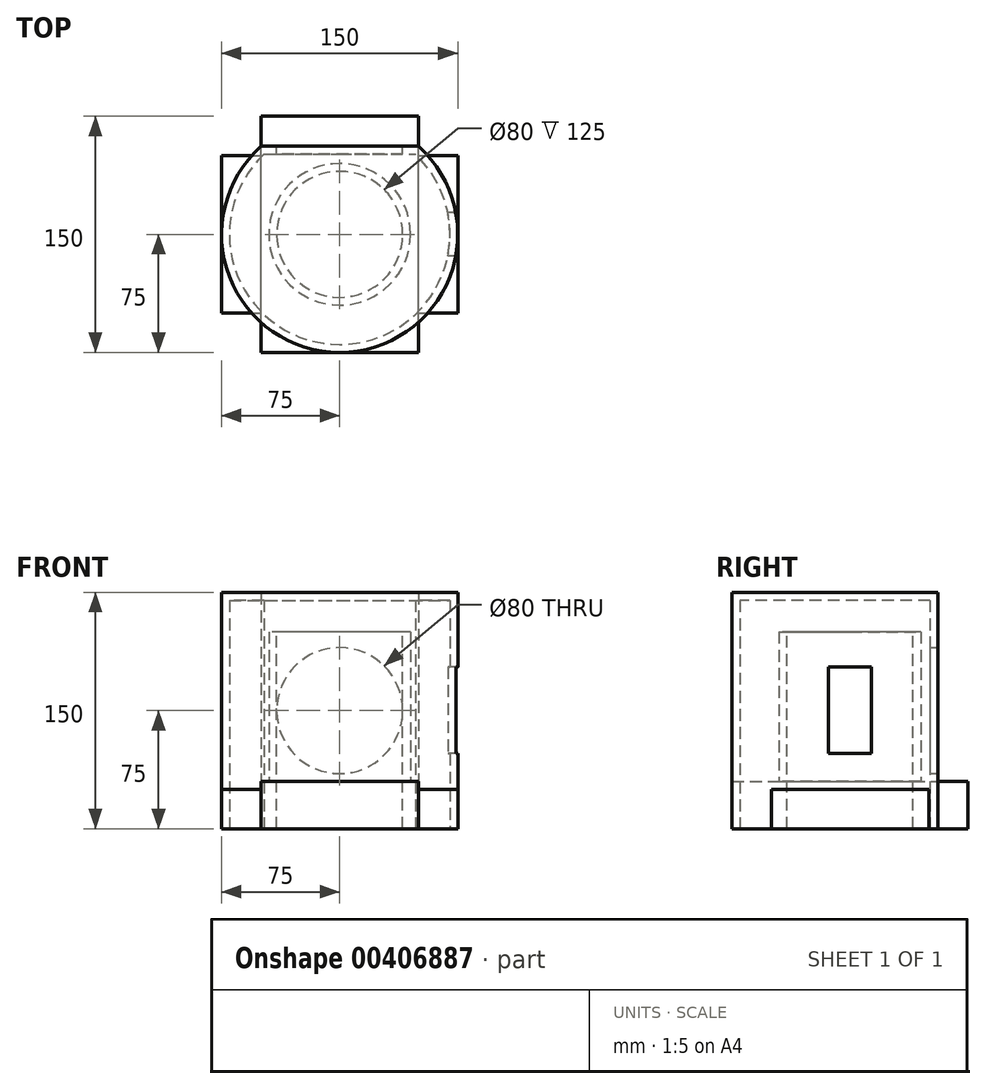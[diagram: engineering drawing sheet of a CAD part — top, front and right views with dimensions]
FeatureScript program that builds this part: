
annotation { "Feature Type Name" : "Feature", "Feature Type Description" : "" }
export const myFeature = defineFeature(function(context is Context, id is Id, definition is map)
    precondition{}
    {
        {
            var Q0;
            Q0=qCreatedBy(makeId("Top.planeOp"),FACE);
            var sketch = newSketch(context, id + "F0", { "sketchPlane" : qUnion([Q0])});
            skArc(sketch, "E0", {"start": v(-50, 55.9) * mm, "mid": v(0, -75) * mm, "end": v(50, 55.9) * mm});
            skLineSegment(sketch, "E1", {"start": v(-50, 55.9) * mm, "end": v(50, 55.9) * mm});
            skSolve(sketch);
        }
        {
            var Q0;
            Q0=qSketchRegion(id+"F0",true);
            extrude(context, id + "F1", {"entities" : qUnion([Q0]), "depth" : 150 * mm});
        }
        {
            var Q0;
            Q0=makeQuery(id+"F1.opExtrude","CAP_FACE",FACE,{"disambiguationData":[OSD([sQuery(id+"F0.wireOp",EDGE,"E0")])],"isStart":true});
            shell(context, id + "F2", {"entities" : qUnion([Q0]), "thickness" : 5 * mm});
        }
        {
            var Q0;
            Q0=makeQuery(id+"F1.opExtrude","SWEPT_FACE",FACE,{"disambiguationData":[OSD([sQuery(id+"F0.wireOp",EDGE,"E1")])]});
            var sketch = newSketch(context, id + "F3", { "sketchPlane" : qUnion([Q0])});
            skPoint(sketch, "E2.endSnap0", {"position": v(0, 0) * mm});
            skCircle(sketch, "E3", {"center": v(0, 75) * mm, "radius": 40 * mm});
            skLineSegment(sketch, "E4", {"start": v(0, 115) * mm, "end": v(0, 150) * mm});
            skSolve(sketch);
        }
        {
            var Q0;
            Q0=qSketchRegion(id+"F3",true);
            extrude(context, id + "F4", {"entities" : qUnion([Q0]), "operationType" : NewBodyOperationType.REMOVE, "oppositeDirection" : true, "depth" : 25 * mm});
        }
        {
            var Q0;
            Q0=qCreatedBy(makeId("Top.planeOp"),FACE);
            var sketch = newSketch(context, id + "F5", { "sketchPlane" : qUnion([Q0])});
            skLineSegment(sketch, "E5.bottom", {"start": v(-50, -75) * mm, "end": v(50, -75) * mm});
            skLineSegment(sketch, "E5.top", {"start": v(-50, 75) * mm, "end": v(50, 75) * mm});
            skLineSegment(sketch, "E5.left", {"start": v(-50, -75) * mm, "end": v(-50, 75) * mm});
            skLineSegment(sketch, "E5.right", {"start": v(50, -75) * mm, "end": v(50, 75) * mm});
            skPoint(sketch, "E5.middle", {"position": v(0, 0) * mm});
            skSolve(sketch);
        }
        {
            var Q0;
            Q0=qSketchRegion(id+"F5",true);
            extrude(context, id + "F6", {"entities" : qUnion([Q0]), "depth" : 30 * mm});
        }
        {
            var Q0;
            Q0=makeQuery(id+"F6.opExtrude","CAP_FACE",FACE,{"disambiguationData":[OSD([sQuery(id+"F5.wireOp",EDGE,"E5.bottom"),sQuery(id+"F5.wireOp",EDGE,"E5.top"),sQuery(id+"F5.wireOp",EDGE,"E5.left"),sQuery(id+"F5.wireOp",EDGE,"E5.right")])],"isStart":false});
            var sketch = newSketch(context, id + "F7", { "sketchPlane" : qUnion([Q0])});
            skCircle(sketch, "E6", {"center": v(0, 0) * mm, "radius": 40 * mm});
            skSolve(sketch);
        }
        {
            var Q0;
            Q0=qSketchRegion(id+"F7",true);
            extrude(context, id + "F8", {"entities" : qUnion([Q0]), "operationType" : NewBodyOperationType.REMOVE, "oppositeDirection" : true, "depth" : 30 * mm});
        }
        {
            var Q0;
            Q0=qCreatedBy(makeId("Right.planeOp"),FACE);
            var sketch = newSketch(context, id + "F9", { "sketchPlane" : qUnion([Q0])});
            skLineSegment(sketch, "E7.bottom", {"start": v(-13.75, 102.66) * mm, "end": v(13.75, 102.66) * mm});
            skLineSegment(sketch, "E7.top", {"start": v(-13.75, 47.66) * mm, "end": v(13.75, 47.66) * mm});
            skLineSegment(sketch, "E7.left", {"start": v(-13.75, 102.66) * mm, "end": v(-13.75, 47.66) * mm});
            skLineSegment(sketch, "E7.right", {"start": v(13.75, 102.66) * mm, "end": v(13.75, 47.66) * mm});
            skPoint(sketch, "E7.middle", {"position": v(0, 75.16) * mm});
            skSolve(sketch);
        }
        {
            var Q0;
            Q0=qSketchRegion(id+"F9",true);
            extrude(context, id + "F10", {"entities" : qUnion([Q0]), "operationType" : NewBodyOperationType.REMOVE, "oppositeDirection" : true, "depth" : -100 * mm});
        }
        {
            var Q0;
            Q0=qCreatedBy(makeId("Top.planeOp"),FACE);
            var sketch = newSketch(context, id + "F11", { "sketchPlane" : qUnion([Q0])});
            skLineSegment(sketch, "E8.bottom", {"start": v(-75, -50) * mm, "end": v(75, -50) * mm});
            skLineSegment(sketch, "E8.top", {"start": v(-75, 50) * mm, "end": v(75, 50) * mm});
            skLineSegment(sketch, "E8.left", {"start": v(-75, -50) * mm, "end": v(-75, 50) * mm});
            skLineSegment(sketch, "E8.right", {"start": v(75, -50) * mm, "end": v(75, 50) * mm});
            skPoint(sketch, "E8.middle", {"position": v(0, 0) * mm});
            skCircle(sketch, "E9", {"center": v(0, 0) * mm, "radius": 40 * mm});
            skCircle(sketch, "E10.0", {"center": v(0, 0) * mm, "radius": 45 * mm});
            skSolve(sketch);
        }
        {
            var Q0;
            Q0=qSketchRegion(id+"F11",true);
            extrude(context, id + "F12", {"entities" : qUnion([Q0]), "depth" : 25 * mm});
        }
        {
            var Q0;
            Q0=makeQuery(id+"F11.imprint","IMPRINT",FACE,{"disambiguationData":[TD([[makeQuery(id+"F11.imprint","IMPRINT",EDGE,{"derivedFrom":sQuery(id+"F11.wireOp",EDGE,"E9")}),-1.0]])]});
            extrude(context, id + "F13", {"entities" : qUnion([Q0]), "operationType" : NewBodyOperationType.ADD, "depth" : 125 * mm});
        }
    });
